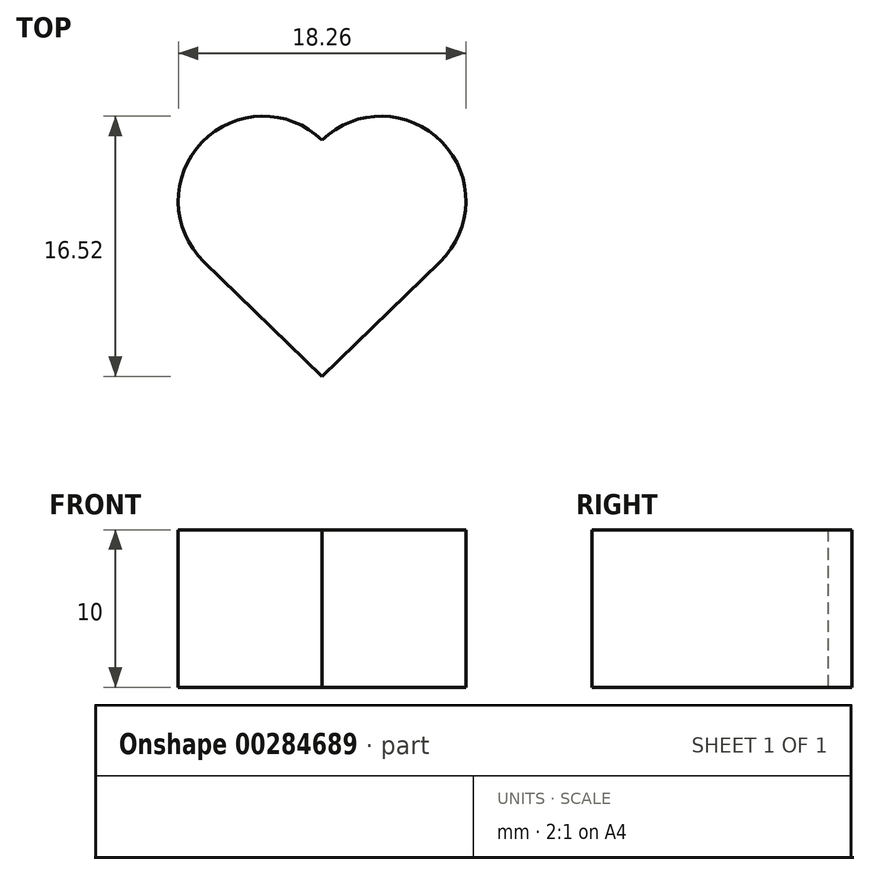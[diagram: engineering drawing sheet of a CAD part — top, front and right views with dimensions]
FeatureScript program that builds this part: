
annotation { "Feature Type Name" : "Feature", "Feature Type Description" : "" }
export const myFeature = defineFeature(function(context is Context, id is Id, definition is map)
    precondition{}
    {
        {
            var Q0;
            Q0=qCreatedBy(makeId("Top.planeOp"),FACE);
            var sketch = newSketch(context, id + "F0", { "sketchPlane" : qUnion([Q0])});
            skLineSegment(sketch, "E0", {"start": v(0, -7.27) * mm, "end": v(7.5, 0) * mm});
            skArc(sketch, "E1", {"start": v(7.5, 0) * mm, "mid": v(7.62, 7.62) * mm, "end": v(0, 7.73) * mm});
            skArc(sketch, "E2.MirrorCS", {"start": v(-7.5, 0) * mm, "mid": v(-7.62, 7.62) * mm, "end": v(0, 7.73) * mm});
            skLineSegment(sketch, "E3.MirrorCS", {"start": v(0, -7.27) * mm, "end": v(-7.5, 0) * mm});
            skSolve(sketch);
        }
        {
            var Q0;
            Q0=makeQuery(id+"F0.imprint","IMPRINT",FACE,{"disambiguationData":[TD([[makeQuery(id+"F0.imprint","IMPRINT",EDGE,{"derivedFrom":sQuery(id+"F0.wireOp",EDGE,"E0")}),1.0]])]});
            extrude(context, id + "F1", {"entities" : qUnion([Q0]), "depth" : 10 * mm});
        }
    });
